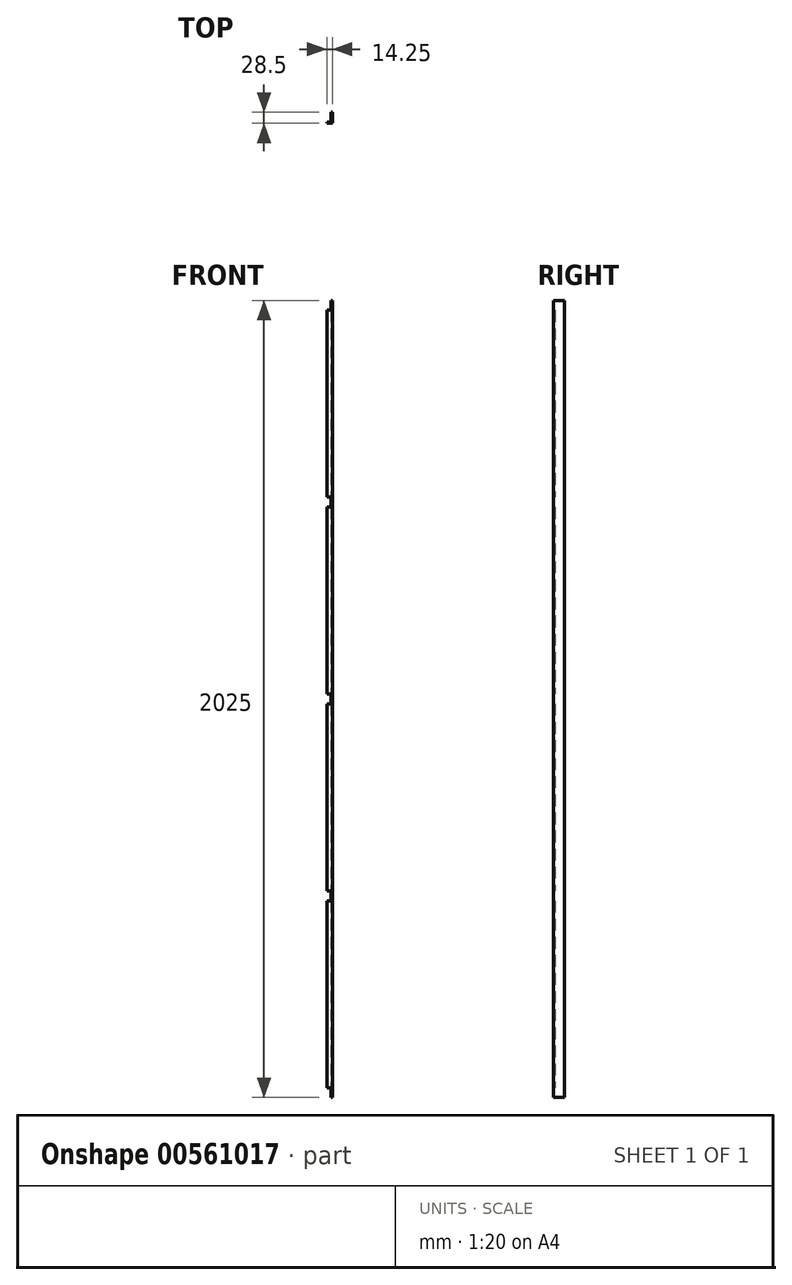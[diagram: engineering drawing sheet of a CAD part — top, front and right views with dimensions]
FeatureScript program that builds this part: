
annotation { "Feature Type Name" : "Feature", "Feature Type Description" : "" }
export const myFeature = defineFeature(function(context is Context, id is Id, definition is map)
    precondition{}
    {
        {
            var Q0;
            Q0=qCreatedBy(makeId("Top.planeOp"),FACE);
            var sketch = newSketch(context, id + "F0", { "sketchPlane" : qUnion([Q0])});
            skLineSegment(sketch, "E0", {"start": v(-14.25, -3.5) * mm, "end": v(10.75, -3.5) * mm});
            skLineSegment(sketch, "E1", {"start": v(10.75, -3.5) * mm, "end": v(10.75, 0) * mm});
            skLineSegment(sketch, "E2", {"start": v(10.75, 0) * mm, "end": v(0, 0) * mm});
            skLineSegment(sketch, "E3", {"start": v(0, 0) * mm, "end": v(0, 25) * mm});
            skLineSegment(sketch, "E4", {"start": v(0, 25) * mm, "end": v(-3.5, 25) * mm});
            skLineSegment(sketch, "E5", {"start": v(-3.5, 25) * mm, "end": v(-3.5, 0) * mm});
            skLineSegment(sketch, "E6", {"start": v(-14.25, 0) * mm, "end": v(-14.25, -3.5) * mm});
            skLineSegment(sketch, "E7", {"start": v(-3.5, 0) * mm, "end": v(-14.25, 0) * mm});
            skSolve(sketch);
        }
        {
            var Q0;
            Q0=qSketchRegion(id+"F0",true);
            extrude(context, id + "F1", {"entities" : qUnion([Q0]), "depth" : 2025 * mm, "offsetDistance" : 25 * mm});
        }
        {
            var Q0;
            Q0=makeQuery(id+"F1.opExtrude","SWEPT_FACE",FACE,{"disambiguationData":[OSD([sQuery(id+"F0.wireOp",EDGE,"E7")])]});
            var sketch = newSketch(context, id + "F2", { "sketchPlane" : qUnion([Q0])});
            skLineSegment(sketch, "E8.bottom", {"start": v(14.25, 0) * mm, "end": v(3.5, 0) * mm});
            skLineSegment(sketch, "E8.top", {"start": v(14.25, 25) * mm, "end": v(3.5, 25) * mm});
            skLineSegment(sketch, "E8.left", {"start": v(14.25, 0) * mm, "end": v(14.25, 25) * mm});
            skLineSegment(sketch, "E8.right", {"start": v(3.5, 0) * mm, "end": v(3.5, 25) * mm});
            skLineSegment(sketch, "E9.bottom", {"start": v(0, 0) * mm, "end": v(-10.75, 0) * mm});
            skLineSegment(sketch, "E9.top", {"start": v(0, 25) * mm, "end": v(-10.75, 25) * mm});
            skLineSegment(sketch, "E9.left", {"start": v(0, 0) * mm, "end": v(0, 25) * mm});
            skLineSegment(sketch, "E9.right", {"start": v(-10.75, 0) * mm, "end": v(-10.75, 25) * mm});
            skLineSegment(sketch, "E10.bottom", {"start": v(3.5, 2025) * mm, "end": v(14.25, 2025) * mm});
            skLineSegment(sketch, "E10.top", {"start": v(3.5, 2000) * mm, "end": v(14.25, 2000) * mm});
            skLineSegment(sketch, "E10.left", {"start": v(3.5, 2025) * mm, "end": v(3.5, 2000) * mm});
            skLineSegment(sketch, "E10.right", {"start": v(14.25, 2025) * mm, "end": v(14.25, 2000) * mm});
            skLineSegment(sketch, "E11.bottom", {"start": v(0, 2000) * mm, "end": v(-10.75, 2000) * mm});
            skLineSegment(sketch, "E11.top", {"start": v(0, 2025) * mm, "end": v(-10.75, 2025) * mm});
            skLineSegment(sketch, "E11.left", {"start": v(0, 2000) * mm, "end": v(0, 2025) * mm});
            skLineSegment(sketch, "E11.right", {"start": v(-10.75, 2000) * mm, "end": v(-10.75, 2025) * mm});
            skLineSegment(sketch, "E12.bottom", {"start": v(3.5, 1525) * mm, "end": v(14.25, 1525) * mm});
            skLineSegment(sketch, "E12.top", {"start": v(3.5, 1500) * mm, "end": v(14.25, 1500) * mm});
            skLineSegment(sketch, "E12.left", {"start": v(3.5, 1525) * mm, "end": v(3.5, 1500) * mm});
            skLineSegment(sketch, "E12.right", {"start": v(14.25, 1525) * mm, "end": v(14.25, 1500) * mm});
            skLineSegment(sketch, "E13.bottom", {"start": v(0, 1525) * mm, "end": v(-10.75, 1525) * mm});
            skLineSegment(sketch, "E13.top", {"start": v(0, 1500) * mm, "end": v(-10.75, 1500) * mm});
            skLineSegment(sketch, "E13.left", {"start": v(0, 1525) * mm, "end": v(0, 1500) * mm});
            skLineSegment(sketch, "E13.right", {"start": v(-10.75, 1525) * mm, "end": v(-10.75, 1500) * mm});
            skLineSegment(sketch, "E14.bottom", {"start": v(14.25, 1025) * mm, "end": v(3.5, 1025) * mm});
            skLineSegment(sketch, "E14.top", {"start": v(14.25, 1000) * mm, "end": v(3.5, 1000) * mm});
            skLineSegment(sketch, "E14.left", {"start": v(14.25, 1025) * mm, "end": v(14.25, 1000) * mm});
            skLineSegment(sketch, "E14.right", {"start": v(3.5, 1025) * mm, "end": v(3.5, 1000) * mm});
            skLineSegment(sketch, "E15.bottom", {"start": v(0, 1000) * mm, "end": v(-10.75, 1000) * mm});
            skLineSegment(sketch, "E15.top", {"start": v(0, 1025) * mm, "end": v(-10.75, 1025) * mm});
            skLineSegment(sketch, "E15.left", {"start": v(0, 1000) * mm, "end": v(0, 1025) * mm});
            skLineSegment(sketch, "E15.right", {"start": v(-10.75, 1000) * mm, "end": v(-10.75, 1025) * mm});
            skLineSegment(sketch, "E16", {"start": v(-10.75, 1012.5) * mm, "end": v(-10.75, 1512.5) * mm});
            skLineSegment(sketch, "E17", {"start": v(-10.75, 1512.5) * mm, "end": v(-10.75, 2012.5) * mm});
            skLineSegment(sketch, "E18.bottom", {"start": v(3.5, 525) * mm, "end": v(14.25, 525) * mm});
            skLineSegment(sketch, "E18.top", {"start": v(3.5, 500) * mm, "end": v(14.25, 500) * mm});
            skLineSegment(sketch, "E18.left", {"start": v(3.5, 525) * mm, "end": v(3.5, 500) * mm});
            skLineSegment(sketch, "E18.right", {"start": v(14.25, 525) * mm, "end": v(14.25, 500) * mm});
            skLineSegment(sketch, "E19.bottom", {"start": v(0, 525) * mm, "end": v(-10.75, 525) * mm});
            skLineSegment(sketch, "E19.top", {"start": v(0, 500) * mm, "end": v(-10.75, 500) * mm});
            skLineSegment(sketch, "E19.left", {"start": v(0, 525) * mm, "end": v(0, 500) * mm});
            skLineSegment(sketch, "E19.right", {"start": v(-10.75, 525) * mm, "end": v(-10.75, 500) * mm});
            skLineSegment(sketch, "E20", {"start": v(-10.75, 1012.5) * mm, "end": v(-10.75, 512.5) * mm});
            skLineSegment(sketch, "E21", {"start": v(-10.75, 512.5) * mm, "end": v(-10.75, 12.5) * mm});
            skSolve(sketch);
        }
        {
            var Q0;
            Q0=qSketchRegion(id+"F2",true);
            extrude(context, id + "F3", {"entities" : qUnion([Q0]), "operationType" : NewBodyOperationType.REMOVE, "endBound" : BoundingType.THROUGH_ALL, "oppositeDirection" : true, "depth" : 25 * mm, "offsetDistance" : 25 * mm});
        }
        {
            var Q0;
            Q0=makeQuery(id+"F3.boolean.opBoolean","COPY",FACE,{"derivedFrom":makeQuery(id+"F3.opExtrude","SWEPT_FACE",FACE,{"disambiguationData":[OSD([sQuery(id+"F2.wireOp",EDGE,"E11.bottom")])]})});
            var sketch = newSketch(context, id + "F4", { "sketchPlane" : qUnion([Q0])});
            skLineSegment(sketch, "E22.bottom", {"start": v(0, 0) * mm, "end": v(10.75, 0) * mm});
            skLineSegment(sketch, "E22.top", {"start": v(0, -3.5) * mm, "end": v(10.75, -3.5) * mm});
            skLineSegment(sketch, "E22.left", {"start": v(0, 0) * mm, "end": v(0, -3.5) * mm});
            skLineSegment(sketch, "E22.right", {"start": v(10.75, 0) * mm, "end": v(10.75, -3.5) * mm});
            skSolve(sketch);
        }
        {
            var Q0;
            Q0 = qSketchRegion(id + "F4", true);
            extrude(context, id + "F5", {"entities" : qUnion([Q0]), "operationType" : NewBodyOperationType.REMOVE, "endBound" : BoundingType.THROUGH_ALL, "oppositeDirection" : true, "depth" : 25 * mm, "offsetDistance" : 25 * mm});
        }
    });
